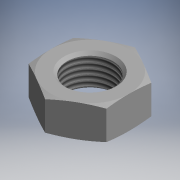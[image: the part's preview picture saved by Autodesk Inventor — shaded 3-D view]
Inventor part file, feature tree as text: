
AUTODESK INVENTOR PART (.ipt)
format: ipt  version: 2017.3 (Build 213256000, 256)  size: 154,624 bytes
history: native  units: mm (DEFAULTED — no unit token found)
features: other x70, sketch x3, revolve x2, extrude x1, thread x1
ambient origin geometry x8: Origin, YZ Plane, XZ Plane, XY Plane, X Axis, Y Axis, Z Axis, Center Point
bodies: Solid1 (feature_tree)
feature tree (77):
  sketch  "Sketch_8"  dims[d0=360.0deg d1=7.874mm d2=0.0mm]
  sketch  "Sketch_10"  dims[d3=360.0deg d4=6.49986mm d5=0.0mm]
  revolve  "Revolution1"  [1 undecoded]
  extrude  "Extrusion1"  Depth=6.49986mm TaperAngle=0.0deg
  revolve  "Revolution2"  [1 undecoded]
  thread  "Thread1"  [1 undecoded]
  other  "NUT_XY"
  other  "NUT_YZ"
  other  "NUT_ZX"
  other  "NUT_X"
  other  "NUT_Y"
  other  "NUT_Z"
  other  "NUT_Center"
  other  "a1_XY"
  other  "a1_YZ"
  other  "a1_ZX"
  other  "a1_X"
  other  "a1_Y"
  other  "a1_Z"
  other  "a1_Center"
  other  "a2_XY"
  other  "a2_YZ"
  other  "a2_ZX"
  other  "a2_X"
  other  "a2_Y"
  other  "a2_Z"
  other  "a2_Center"
  other  "b1_XY"
  other  "b1_YZ"
  other  "b1_ZX"
  other  "b1_X"
  other  "b1_Y"
  other  "b1_Z"
  other  "b1_Center"
  other  "b2_XY"
  other  "b2_YZ"
  other  "b2_ZX"
  other  "b2_X"
  other  "b2_Y"
  other  "b2_Z"
  other  "b2_Center"
  other  "e_XY"
  other  "e_YZ"
  other  "e_ZX"
  other  "e_X"
  other  "e_Y"
  other  "e_Z"
  other  "e_Center"
  other  "ol1_XY"
  other  "ol1_YZ"
  other  "ol1_ZX"
  other  "ol1_X"
  other  "ol1_Y"
  other  "ol1_Z"
  other  "ol1_Center"
  other  "ol2_XY"
  other  "ol2_YZ"
  other  "ol2_ZX"
  other  "ol2_X"
  other  "ol2_Y"
  other  "ol2_Z"
  other  "ol2_Center"
  other  "th1_XY"
  other  "th1_YZ"
  other  "th1_ZX"
  other  "th1_X"
  other  "th1_Y"
  other  "th1_Z"
  other  "th1_Center"
  other  "th2_XY"
  other  "th2_YZ"
  other  "th2_ZX"
  other  "th2_X"
  other  "th2_Y"
  other  "th2_Z"
  other  "th2_Center"
  sketch  "Sketch_11"  dims[d6=0.0mm d7=0.0mm d8=0.0mm]
note: 3 required parameter values undecoded (feature->parameter linkage not recoverable at this tier; creation-order binding heuristic only, values carry confidence <= 0.55)